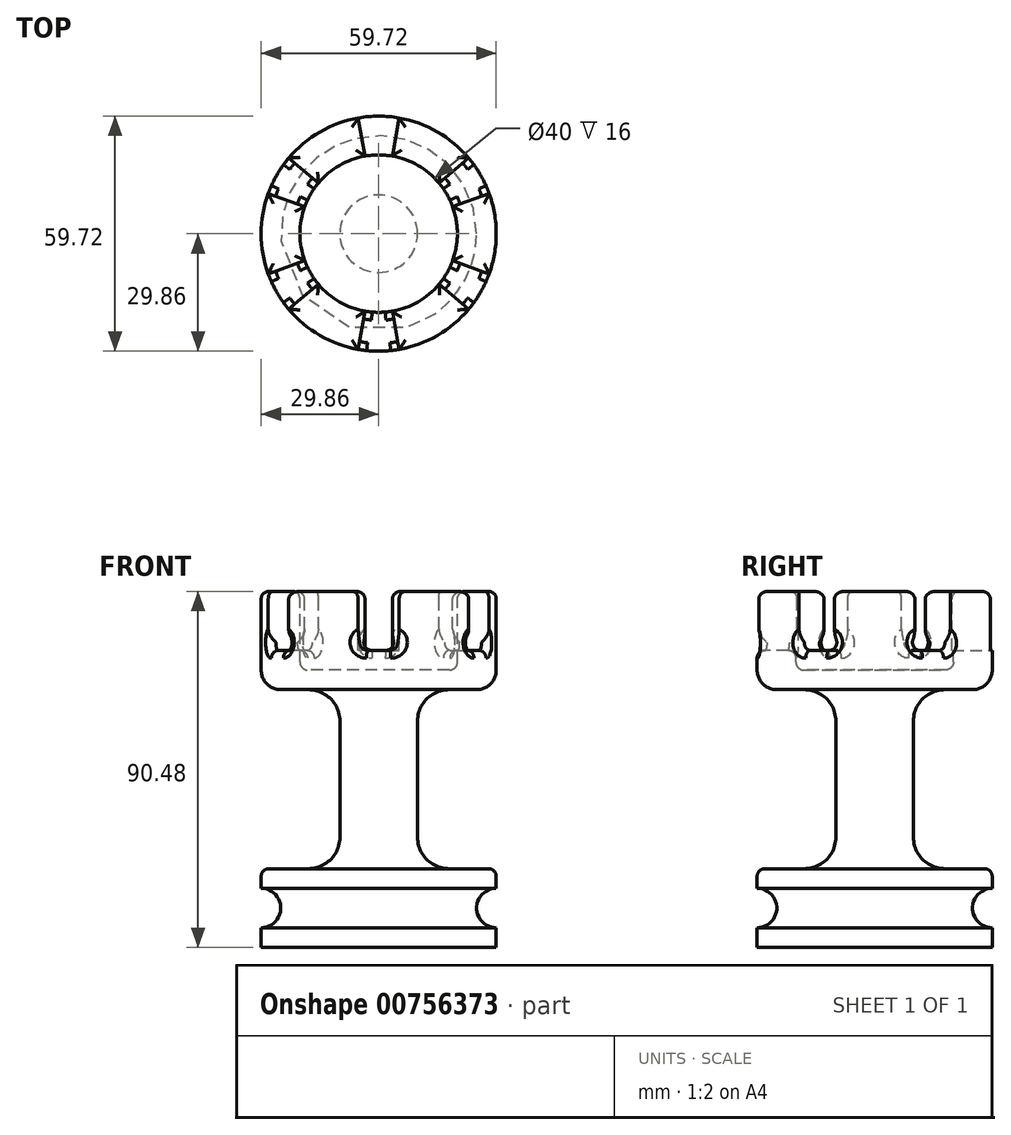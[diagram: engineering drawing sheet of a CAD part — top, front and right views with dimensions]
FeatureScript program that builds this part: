
annotation { "Feature Type Name" : "Feature", "Feature Type Description" : "" }
export const myFeature = defineFeature(function(context is Context, id is Id, definition is map)
    precondition{}
    {
        {
            var Q0;
            Q0=qCreatedBy(makeId("Front.planeOp"),FACE);
            var sketch = newSketch(context, id + "F0", { "sketchPlane" : qUnion([Q0])});
            skLineSegment(sketch, "E0.top", {"start": v(9.86, 20) * mm, "end": v(29.86, 20) * mm});
            skLineSegment(sketch, "E0.right", {"start": v(29.86, 0) * mm, "end": v(29.86, 5) * mm});
            skLineSegment(sketch, "E1.right", {"start": v(9.86, 20) * mm, "end": v(9.86, 65.48) * mm});
            skLineSegment(sketch, "E2.bottom", {"start": v(9.86, 65.48) * mm, "end": v(29.86, 65.48) * mm});
            skLineSegment(sketch, "E2.top", {"start": v(0, 90.48) * mm, "end": v(29.86, 90.48) * mm});
            skLineSegment(sketch, "E2.right", {"start": v(29.86, 65.48) * mm, "end": v(29.86, 90.48) * mm});
            skLineSegment(sketch, "E3", {"start": v(0, 90.48) * mm, "end": v(0, 0) * mm});
            skLineSegment(sketch, "E4", {"start": v(0, 0) * mm, "end": v(29.86, 0) * mm});
            skArc(sketch, "E5", {"start": v(29.86, 15) * mm, "mid": v(24.86, 10) * mm, "end": v(29.86, 5) * mm});
            skLineSegment(sketch, "E6.trimOffspring", {"start": v(29.86, 15) * mm, "end": v(29.86, 20) * mm});
            skSolve(sketch);
        }
        {
            var Q0;
            Q0 = qSketchRegion(id + "F0", true);
            var Q1;
            Q1=sQuery(id+"F0.wireOp",EDGE,"E3");
            revolve(context, id + "F1", {"surfaceOperationType" : NewSurfaceOperationType.NEW, "entities" : qUnion([Q0]), "axis" : qUnion([Q1]), "revolveType" : RevolveType.FULL});
        }
        {
            var Q0;
            Q0=makeQuery(id+"F1.opRevolve","SWEPT_FACE",FACE,{"disambiguationData":[OSD([sQuery(id+"F0.wireOp",EDGE,"E2.top")])]});
            var sketch = newSketch(context, id + "F2", { "sketchPlane" : qUnion([Q0])});
            skCircle(sketch, "E7", {"center": v(0, 0) * mm, "radius": 20 * mm});
            skSolve(sketch);
        }
        {
            var Q0;
            Q0 = qSketchRegion(id + "F2", true);
            extrude(context, id + "F3", {"entities" : qUnion([Q0]), "operationType" : NewBodyOperationType.REMOVE, "oppositeDirection" : true, "depth" : 20 * mm, "offsetDistance" : 25 * mm});
        }
        {
            var Q0;
            Q0=makeQuery(id+"F1.opRevolve","SWEPT_FACE",FACE,{"disambiguationData":[OSD([sQuery(id+"F0.wireOp",EDGE,"E2.top")])]});
            var sketch = newSketch(context, id + "F4", { "sketchPlane" : qUnion([Q0])});
            skLineSegment(sketch, "E8", {"start": v(3.47, 19.7) * mm, "end": v(5.2, 29.54) * mm});
            skLineSegment(sketch, "E9", {"start": v(-3.47, 19.7) * mm, "end": v(-5.2, 29.54) * mm});
            skArc(sketch, "E10", {"start": v(5.2, 29.54) * mm, "mid": v(0, 30) * mm, "end": v(-5.2, 29.54) * mm});
            skArc(sketch, "E11", {"start": v(3.47, 19.7) * mm, "mid": v(0, 20) * mm, "end": v(-3.47, 19.7) * mm});
            skLineSegment(sketch, "E12.1.0", {"start": v(-18.8, 6.84) * mm, "end": v(-28.2, 10.26) * mm});
            skArc(sketch, "E12.1.1", {"start": v(-15.32, 12.86) * mm, "mid": v(-17.32, 10) * mm, "end": v(-18.8, 6.84) * mm});
            skLineSegment(sketch, "E12.1.2", {"start": v(-15.32, 12.86) * mm, "end": v(-22.98, 19.28) * mm});
            skArc(sketch, "E12.1.3", {"start": v(-22.98, 19.28) * mm, "mid": v(-25.98, 15) * mm, "end": v(-28.2, 10.26) * mm});
            skLineSegment(sketch, "E12.2.0", {"start": v(-15.32, -12.86) * mm, "end": v(-22.98, -19.28) * mm});
            skArc(sketch, "E12.2.1", {"start": v(-18.8, -6.84) * mm, "mid": v(-17.32, -10) * mm, "end": v(-15.32, -12.86) * mm});
            skLineSegment(sketch, "E12.2.2", {"start": v(-18.8, -6.84) * mm, "end": v(-28.2, -10.26) * mm});
            skArc(sketch, "E12.2.3", {"start": v(-28.2, -10.26) * mm, "mid": v(-25.98, -15) * mm, "end": v(-22.98, -19.28) * mm});
            skLineSegment(sketch, "E12.3.0", {"start": v(3.47, -19.7) * mm, "end": v(5.2, -29.54) * mm});
            skArc(sketch, "E12.3.1", {"start": v(-3.47, -19.7) * mm, "mid": v(0, -20) * mm, "end": v(3.47, -19.7) * mm});
            skLineSegment(sketch, "E12.3.2", {"start": v(-3.47, -19.7) * mm, "end": v(-5.2, -29.54) * mm});
            skArc(sketch, "E12.3.3", {"start": v(-5.2, -29.54) * mm, "mid": v(0, -30) * mm, "end": v(5.2, -29.54) * mm});
            skLineSegment(sketch, "E12.4.0", {"start": v(18.8, -6.84) * mm, "end": v(28.2, -10.26) * mm});
            skArc(sketch, "E12.4.1", {"start": v(15.32, -12.86) * mm, "mid": v(17.32, -10) * mm, "end": v(18.8, -6.84) * mm});
            skLineSegment(sketch, "E12.4.2", {"start": v(15.32, -12.86) * mm, "end": v(22.98, -19.28) * mm});
            skArc(sketch, "E12.4.3", {"start": v(22.98, -19.28) * mm, "mid": v(25.98, -15) * mm, "end": v(28.2, -10.26) * mm});
            skLineSegment(sketch, "E12.5.0", {"start": v(15.32, 12.86) * mm, "end": v(22.98, 19.28) * mm});
            skArc(sketch, "E12.5.1", {"start": v(18.8, 6.84) * mm, "mid": v(17.32, 10) * mm, "end": v(15.32, 12.86) * mm});
            skLineSegment(sketch, "E12.5.2", {"start": v(18.8, 6.84) * mm, "end": v(28.2, 10.26) * mm});
            skArc(sketch, "E12.5.3", {"start": v(28.2, 10.26) * mm, "mid": v(25.98, 15) * mm, "end": v(22.98, 19.28) * mm});
            skSolve(sketch);
        }
        {
            var Q0;
            Q0 = qSketchRegion(id + "F4", true);
            extrude(context, id + "F5", {"entities" : qUnion([Q0]), "operationType" : NewBodyOperationType.REMOVE, "oppositeDirection" : true, "depth" : 15 * mm, "offsetDistance" : 25 * mm});
        }
        {
            var Q0;
            Q0=makeQuery(id+"F1.opRevolve","SWEPT_FACE",FACE,{"disambiguationData":[OSD([sQuery(id+"F0.wireOp",EDGE,"E1.right")])]});
            fillet(context, id + "F6", {"entities" : qUnion([Q0]), "radius" : 8 * mm, "tangentPropagation" : true, "allowEdgeOverflow" : false});
        }
        {
            var Q0;
            Q0=makeQuery(id+"F1.opRevolve","SWEPT_EDGE",EDGE,{"disambiguationData":[OSD([sQuery(id+"F0.wireOp",EDGE,"E2.bottom"),sQuery(id+"F0.wireOp",EDGE,"E2.right")])]});
            fillet(context, id + "F7", {"entities" : qUnion([Q0]), "radius" : 5 * mm, "tangentPropagation" : true, "allowEdgeOverflow" : false});
        }
        {
            var Q0;
            Q0=makeQuery(id+"F1.opRevolve","SWEPT_EDGE",EDGE,{"disambiguationData":[OSD([sQuery(id+"F0.wireOp",EDGE,"E0.top"),sQuery(id+"F0.wireOp",EDGE,"E6.trimOffspring")])]});
            var Q1;
            Q1=makeQuery(id+"F5.boolean.opBoolean","SPLIT",FACE,{"disambiguationData":[TD([makeQuery(id+"F5.opExtrude","SWEPT_FACE",FACE,{"disambiguationData":[OSD([sQuery(id+"F4.wireOp",EDGE,"E12.3.0")])]})])],"derivedFrom":makeQuery(id+"F1.opRevolve","SWEPT_FACE",FACE,{"disambiguationData":[OSD([sQuery(id+"F0.wireOp",EDGE,"E2.top")])]})});
            var Q2;
            Q2=makeQuery(id+"F5.boolean.opBoolean","SPLIT",FACE,{"disambiguationData":[TD([makeQuery(id+"F5.opExtrude","SWEPT_FACE",FACE,{"disambiguationData":[OSD([sQuery(id+"F4.wireOp",EDGE,"E12.4.0")])]})])],"derivedFrom":makeQuery(id+"F1.opRevolve","SWEPT_FACE",FACE,{"disambiguationData":[OSD([sQuery(id+"F0.wireOp",EDGE,"E2.top")])]})});
            var Q3;
            Q3=makeQuery(id+"F5.boolean.opBoolean","SPLIT",FACE,{"disambiguationData":[TD([makeQuery(id+"F5.opExtrude","SWEPT_FACE",FACE,{"disambiguationData":[OSD([sQuery(id+"F4.wireOp",EDGE,"E8")])]})])],"derivedFrom":makeQuery(id+"F1.opRevolve","SWEPT_FACE",FACE,{"disambiguationData":[OSD([sQuery(id+"F0.wireOp",EDGE,"E2.top")])]})});
            var Q4;
            Q4=makeQuery(id+"F5.boolean.opBoolean","SPLIT",FACE,{"disambiguationData":[TD([makeQuery(id+"F5.opExtrude","SWEPT_FACE",FACE,{"disambiguationData":[OSD([sQuery(id+"F4.wireOp",EDGE,"E9")])]})])],"derivedFrom":makeQuery(id+"F1.opRevolve","SWEPT_FACE",FACE,{"disambiguationData":[OSD([sQuery(id+"F0.wireOp",EDGE,"E2.top")])]})});
            var Q5;
            Q5=makeQuery(id+"F5.boolean.opBoolean","SPLIT",FACE,{"disambiguationData":[TD([makeQuery(id+"F5.opExtrude","SWEPT_FACE",FACE,{"disambiguationData":[OSD([sQuery(id+"F4.wireOp",EDGE,"E12.1.0")])]})])],"derivedFrom":makeQuery(id+"F1.opRevolve","SWEPT_FACE",FACE,{"disambiguationData":[OSD([sQuery(id+"F0.wireOp",EDGE,"E2.top")])]})});
            var Q6;
            Q6=makeQuery(id+"F5.boolean.opBoolean","SPLIT",FACE,{"disambiguationData":[TD([makeQuery(id+"F5.opExtrude","SWEPT_FACE",FACE,{"disambiguationData":[OSD([sQuery(id+"F4.wireOp",EDGE,"E12.2.0")])]})])],"derivedFrom":makeQuery(id+"F1.opRevolve","SWEPT_FACE",FACE,{"disambiguationData":[OSD([sQuery(id+"F0.wireOp",EDGE,"E2.top")])]})});
            var Q7;
            Q7=makeQuery(id+"F3.boolean.opBoolean","COPY",EDGE,{"derivedFrom":makeQuery(id+"F3.opExtrude","CAP_EDGE",EDGE,{"disambiguationData":[OSD([sQuery(id+"F2.wireOp",EDGE,"E7")])],"isStart":false})});
            var Q8;
            Q8=makeQuery(id+"F5.boolean.opBoolean","COPY",FACE,{"derivedFrom":makeQuery(id+"F5.opExtrude","CAP_FACE",FACE,{"disambiguationData":[OSD([sQuery(id+"F4.wireOp",EDGE,"E12.1.0"),sQuery(id+"F4.wireOp",EDGE,"E12.1.1"),sQuery(id+"F4.wireOp",EDGE,"E12.1.2"),sQuery(id+"F4.wireOp",EDGE,"E12.1.3")])],"isStart":false})});
            var Q9;
            Q9=makeQuery(id+"F5.boolean.opBoolean","COPY",EDGE,{"derivedFrom":makeQuery(id+"F5.opExtrude","CAP_EDGE",EDGE,{"disambiguationData":[OSD([sQuery(id+"F4.wireOp",EDGE,"E11")])],"isStart":false})});
            var Q10;
            Q10=makeQuery(id+"F5.boolean.opBoolean","INTERSECT",EDGE,{"derivedFrom":[makeQuery(id+"F1.opRevolve","SWEPT_FACE",FACE,{"disambiguationData":[OSD([sQuery(id+"F0.wireOp",EDGE,"E2.right")])]}),makeQuery(id+"F5.opExtrude","CAP_FACE",FACE,{"disambiguationData":[OSD([sQuery(id+"F4.wireOp",EDGE,"E12.5.0"),sQuery(id+"F4.wireOp",EDGE,"E12.5.1"),sQuery(id+"F4.wireOp",EDGE,"E12.5.2"),sQuery(id+"F4.wireOp",EDGE,"E12.5.3")])],"isStart":false})]});
            var Q11;
            Q11=makeQuery(id+"F5.boolean.opBoolean","COPY",FACE,{"derivedFrom":makeQuery(id+"F5.opExtrude","CAP_FACE",FACE,{"disambiguationData":[OSD([sQuery(id+"F4.wireOp",EDGE,"E12.4.0"),sQuery(id+"F4.wireOp",EDGE,"E12.4.1"),sQuery(id+"F4.wireOp",EDGE,"E12.4.2"),sQuery(id+"F4.wireOp",EDGE,"E12.4.3")])],"isStart":false})});
            var Q12;
            Q12=makeQuery(id+"F5.boolean.opBoolean","COPY",FACE,{"derivedFrom":makeQuery(id+"F5.opExtrude","CAP_FACE",FACE,{"disambiguationData":[OSD([sQuery(id+"F4.wireOp",EDGE,"E12.3.0"),sQuery(id+"F4.wireOp",EDGE,"E12.3.1"),sQuery(id+"F4.wireOp",EDGE,"E12.3.2"),sQuery(id+"F4.wireOp",EDGE,"E12.3.3")])],"isStart":false})});
            var Q13;
            Q13=makeQuery(id+"F5.boolean.opBoolean","COPY",FACE,{"derivedFrom":makeQuery(id+"F5.opExtrude","CAP_FACE",FACE,{"disambiguationData":[OSD([sQuery(id+"F4.wireOp",EDGE,"E12.2.0"),sQuery(id+"F4.wireOp",EDGE,"E12.2.1"),sQuery(id+"F4.wireOp",EDGE,"E12.2.2"),sQuery(id+"F4.wireOp",EDGE,"E12.2.3")])],"isStart":false})});
            var Q14;
            Q14=makeQuery(id+"F5.boolean.opBoolean","COPY",FACE,{"derivedFrom":makeQuery(id+"F5.opExtrude","CAP_FACE",FACE,{"disambiguationData":[OSD([sQuery(id+"F4.wireOp",EDGE,"E12.5.0"),sQuery(id+"F4.wireOp",EDGE,"E12.5.1"),sQuery(id+"F4.wireOp",EDGE,"E12.5.2"),sQuery(id+"F4.wireOp",EDGE,"E12.5.3")])],"isStart":false})});
            fillet(context, id + "F8", {"entities" : qUnion([Q0, Q1, Q2, Q3, Q4, Q5, Q6, Q7, Q8, Q9, Q10, Q11, Q12, Q13, Q14]), "radius" : 2 * mm, "tangentPropagation" : true, "allowEdgeOverflow" : false});
        }
    });
